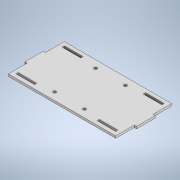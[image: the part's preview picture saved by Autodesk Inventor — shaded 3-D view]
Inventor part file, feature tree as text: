
AUTODESK INVENTOR PART (.ipt)
format: ipt  version: 2020 (Build 240168000, 168)  size: 183,808 bytes
history: native  units: in
note: dims shown in document units (in); Inventor stores cm internally (conversion verified against a paired STEP export)
features: extrude x6, sketch x6
ambient origin geometry x8: Origin, YZ Plane, XZ Plane, XY Plane, X Axis, Y Axis, Z Axis, Center Point
bodies: Solid1 (feature_tree)
feature tree (12):
  extrude  "Extrusion1"  Depth=1.1811in TaperAngle=0.0deg
  extrude  "Extrusion2"  Depth=0.3937in
  extrude  "Extrusion3"  Depth=0.3937in
  extrude  "Extrusion4"  Depth=1.1811in
  extrude  "Extrusion5"  Depth=0.3937in TaperAngle=0.0deg
  extrude  "Extrusion6"  Depth=0.1181in TaperAngle=0.0deg
  sketch  "Sketch1"  dims[d9=0.1181in d10=0.0in d30=1.1811in d31=0.0in]
  sketch  "Sketch2"  dims[d35=0.3937in d36=0.3937in]
  sketch  "Sketch3"  dims[d39=0.3937in d40=0.3937in]
  sketch  "Sketch4"  dims[d41=1.1811in d42=0.0in d43=0.5906in]
  sketch  "Sketch5"  dims[d44=0.5906in d45=0.3937in d46=0.0in]
  sketch  "Sketch6"  dims[d47=0.1181in d48=0.0in d69=0.1181in d70=0.0in d49=0.1969in d50=0.0344in]
